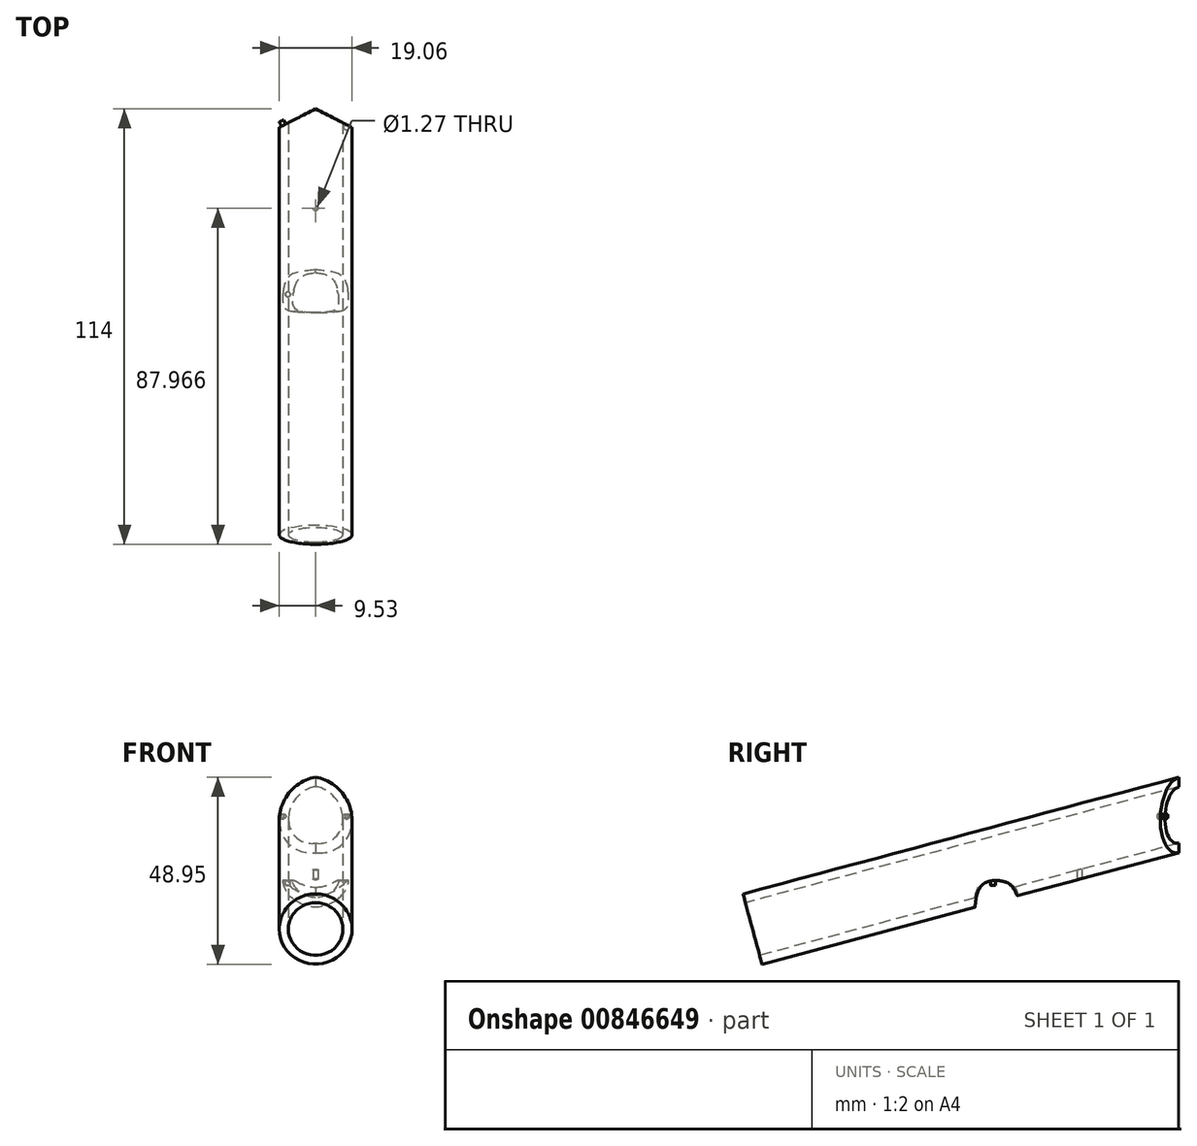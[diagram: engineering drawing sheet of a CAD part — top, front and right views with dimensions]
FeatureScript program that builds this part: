
annotation { "Feature Type Name" : "Feature", "Feature Type Description" : "" }
export const myFeature = defineFeature(function(context is Context, id is Id, definition is map)
    precondition{}
    {
        {
            var Q0;
            Q0=qCreatedBy(makeId("Front.planeOp"),FACE);
            var sketch = newSketch(context, id + "F0", { "sketchPlane" : qUnion([Q0])});
            skLineSegment(sketch, "E0", {"start": v(-25.47, 0) * mm, "end": v(29.78, 0) * mm});
            skSolve(sketch);
        }
        {
            var Q0;
            Q0=sQuery(id+"F0.wireOp",EDGE,"E0");
            cPlane(context, id + "F1", {"entities" : qUnion([Q0]), "cplaneType" : CPlaneType.LINE_ANGLE, "offset" : 25.4 * mm, "angle" : 15 * degree, "width" : 152.4 * mm, "height" : 152.4 * mm});
        }
        {
            var Q0;
            Q0=qCreatedBy(id+"F1.planeOp",FACE);
            var sketch = newSketch(context, id + "F2", { "sketchPlane" : qUnion([Q0])});
            skCircle(sketch, "E1", {"center": v(0, 0) * mm, "radius": 7.14 * mm});
            skCircle(sketch, "E2", {"center": v(0, 0) * mm, "radius": 9.53 * mm});
            skSolve(sketch);
        }
        {
            var Q0;
            Q0=makeQuery(id+"F2.imprint","IMPRINT",FACE,{"disambiguationData":[TD([[makeQuery(id+"F2.imprint","IMPRINT",EDGE,{"derivedFrom":sQuery(id+"F2.wireOp",EDGE,"E1")}),-1.0]])]});
            extrude(context, id + "F3", {"entities" : qUnion([Q0]), "depth" : 120.65 * mm, "offsetDistance" : 25.4 * mm});
        }
        {
            var Q0;
            Q0=qCreatedBy(makeId("Top.planeOp"),FACE);
            var sketch = newSketch(context, id + "F4", { "sketchPlane" : qUnion([Q0])});
            skLineSegment(sketch, "E3", {"start": v(0, 0) * mm, "end": v(0, 139.91) * mm, "construction": true});
            skLineSegment(sketch, "E4", {"start": v(-27.69, 106.68) * mm, "end": v(29.95, 106.68) * mm, "construction": true});
            skLineSegment(sketch, "E5", {"start": v(9.53, 106.68) * mm, "end": v(0, 111.53) * mm});
            skLineSegment(sketch, "E6", {"start": v(0, 111.53) * mm, "end": v(-9.52, 106.68) * mm});
            skLineSegment(sketch, "E7", {"start": v(-9.53, 106.68) * mm, "end": v(-9.53, 132.08) * mm});
            skLineSegment(sketch, "E8", {"start": v(-9.53, 132.08) * mm, "end": v(9.52, 132.08) * mm});
            skLineSegment(sketch, "E9", {"start": v(9.52, 132.08) * mm, "end": v(9.53, 106.68) * mm});
            skSolve(sketch);
        }
        {
            var Q0;
            Q0=qSketchRegion(id+"F4",true);
            extrude(context, id + "F5", {"entities" : qUnion([Q0]), "operationType" : NewBodyOperationType.REMOVE, "depth" : 127 * mm, "offsetDistance" : 25.4 * mm});
        }
        {
            var Q0;
            Q0=qCreatedBy(makeId("Right.planeOp"),FACE);
            var sketch = newSketch(context, id + "F6", { "sketchPlane" : qUnion([Q0])});
            skLineSegment(sketch, "E10", {"start": v(0, 0) * mm, "end": v(63.5, 0) * mm, "construction": true});
            skLineSegment(sketch, "E11", {"start": v(63.5, 0) * mm, "end": v(63.5, 10.16) * mm, "construction": true});
            skSolve(sketch);
        }
        {
            var Q0;
            Q0=qCreatedBy(makeId("Top.planeOp"),FACE);
            var sketch = newSketch(context, id + "F7", { "sketchPlane" : qUnion([Q0])});
            skCircle(sketch, "E12", {"center": v(0, 112.8) * mm, "radius": 54.61 * mm});
            skCircle(sketch, "E13", {"center": v(0, 112.8) * mm, "radius": 43.18 * mm});
            skSolve(sketch);
        }
        {
            var Q0;
            Q0=makeQuery(id+"F7.imprint","IMPRINT",FACE,{"disambiguationData":[TD([[makeQuery(id+"F7.imprint","IMPRINT",EDGE,{"derivedFrom":sQuery(id+"F7.wireOp",EDGE,"E12")}),1.0]])]});
            extrude(context, id + "F8", {"entities" : qUnion([Q0]), "operationType" : NewBodyOperationType.REMOVE, "depth" : 12.7 * mm, "offsetDistance" : 25.4 * mm});
        }
        {
            var Q0;
            Q0=makeQuery(id+"F8.boolean.opBoolean","COPY",EDGE,{"disambiguationData":[OD(0.0)],"derivedFrom":makeQuery(id+"F8.opExtrude","CAP_EDGE",EDGE,{"disambiguationData":[OSD([sQuery(id+"F7.wireOp",EDGE,"E13")])],"isStart":false})});
            var Q1;
            Q1=makeQuery(id+"F8.boolean.opBoolean","COPY",EDGE,{"disambiguationData":[OD(1.0)],"derivedFrom":makeQuery(id+"F8.opExtrude","CAP_EDGE",EDGE,{"disambiguationData":[OSD([sQuery(id+"F7.wireOp",EDGE,"E12")])],"isStart":false})});
            var Q2;
            Q2=makeQuery(id+"F8.boolean.opBoolean","COPY",EDGE,{"disambiguationData":[OD(1.0)],"derivedFrom":makeQuery(id+"F8.opExtrude","CAP_EDGE",EDGE,{"disambiguationData":[OSD([sQuery(id+"F7.wireOp",EDGE,"E13")])],"isStart":false})});
            var Q3;
            Q3=makeQuery(id+"F8.boolean.opBoolean","COPY",EDGE,{"disambiguationData":[OD(0.0)],"derivedFrom":makeQuery(id+"F8.opExtrude","CAP_EDGE",EDGE,{"disambiguationData":[OSD([sQuery(id+"F7.wireOp",EDGE,"E12")])],"isStart":false})});
            fillet(context, id + "F9", {"entities" : qUnion([Q0, Q1, Q2, Q3]), "radius" : 4.76 * mm, "tangentPropagation" : true, "rho" : 0.5, "crossSection" : FilletCrossSection.CONIC, "allowEdgeOverflow" : false});
        }
        {
            var Q0;
            Q0=makeQuery(id+"F5.boolean.opBoolean","COPY",FACE,{"derivedFrom":makeQuery(id+"F5.opExtrude","SWEPT_FACE",FACE,{"disambiguationData":[OSD([sQuery(id+"F4.wireOp",EDGE,"E5")])]})});
            var sketch = newSketch(context, id + "F10", { "sketchPlane" : qUnion([Q0])});
            skCircle(sketch, "E14", {"center": v(41.24, 29.55) * mm, "radius": 0.64 * mm});
            skSolve(sketch);
        }
        {
            var Q0;
            Q0=makeQuery(id+"F10.imprint","IMPRINT",FACE,{"disambiguationData":[TD([[makeQuery(id+"F10.imprint","IMPRINT",EDGE,{"derivedFrom":sQuery(id+"F10.wireOp",EDGE,"E14")}),1.0]])]});
            var Q1;
            Q1=sQuery(id+"F10.wireOp",EDGE,"E14");
            extrude(context, id + "F11", {"entities" : qUnion([Q0]), "operationType" : NewBodyOperationType.REMOVE, "surfaceEntities" : qUnion([Q1]), "oppositeDirection" : true, "depth" : 1.27 * mm, "offsetDistance" : 25.4 * mm});
        }
        {
            var Q0;
            Q0=makeQuery(id+"F5.boolean.opBoolean","COPY",FACE,{"derivedFrom":makeQuery(id+"F5.opExtrude","SWEPT_FACE",FACE,{"disambiguationData":[OSD([sQuery(id+"F4.wireOp",EDGE,"E6")])]})});
            var sketch = newSketch(context, id + "F12", { "sketchPlane" : qUnion([Q0])});
            skCircle(sketch, "E15", {"center": v(-41.24, 29.55) * mm, "radius": 0.64 * mm});
            skSolve(sketch);
        }
        {
            var Q0;
            Q0=makeQuery(id+"F12.imprint","IMPRINT",FACE,{"disambiguationData":[TD([[makeQuery(id+"F12.imprint","IMPRINT",EDGE,{"derivedFrom":sQuery(id+"F12.wireOp",EDGE,"E15")}),1.0]])]});
            extrude(context, id + "F13", {"entities" : qUnion([Q0]), "operationType" : NewBodyOperationType.ADD, "depth" : 1.27 * mm, "offsetDistance" : 25.4 * mm});
        }
        {
            var Q0;
            Q0=makeQuery(id+"F8.boolean.opBoolean","COPY",FACE,{"disambiguationData":[OD(0.0)],"derivedFrom":makeQuery(id+"F8.opExtrude","CAP_FACE",FACE,{"disambiguationData":[OSD([sQuery(id+"F7.wireOp",EDGE,"E12"),sQuery(id+"F7.wireOp",EDGE,"E13")])],"isStart":false})});
            var sketch = newSketch(context, id + "F14", { "sketchPlane" : qUnion([Q0])});
            skCircle(sketch, "E16", {"center": v(-7.26, -62.95) * mm, "radius": 0.64 * mm});
            skSolve(sketch);
        }
        {
            var Q0;
            Q0=qSketchRegion(id+"F14",true);
            extrude(context, id + "F15", {"entities" : qUnion([Q0]), "operationType" : NewBodyOperationType.ADD, "depth" : 1.27 * mm, "offsetDistance" : 25.4 * mm});
        }
        {
            var Q0;
            Q0=qCreatedBy(makeId("Top.planeOp"),FACE);
            var sketch = newSketch(context, id + "F16", { "sketchPlane" : qUnion([Q0])});
            skCircle(sketch, "E17", {"center": v(0, 111.53) * mm, "radius": 38.1 * mm, "construction": true});
            skLineSegment(sketch, "E18", {"start": v(0, 29.2) * mm, "end": v(0, 94.83) * mm, "construction": true});
            skCircle(sketch, "E19", {"center": v(0, 85.5) * mm, "radius": 0.64 * mm});
            skSolve(sketch);
        }
        {
            var Q0;
            Q0=makeQuery(id+"F16.imprint","IMPRINT",FACE,{"disambiguationData":[TD([[makeQuery(id+"F16.imprint","IMPRINT",EDGE,{"derivedFrom":sQuery(id+"F16.wireOp",EDGE,"E19")}),1.0]])]});
            extrude(context, id + "F17", {"entities" : qUnion([Q0]), "operationType" : NewBodyOperationType.REMOVE, "depth" : 19.05 * mm, "offsetDistance" : 25.4 * mm});
        }
    });
